# Revit family: 00-7906-05-00
name_source: partatom
category: Luminarias
revit_build: Autodesk Revit 2017 (Build: 20160225_1515(x64)
units: mm (PartAtom-declared; Revit-internal decimal feet)

## family parameters
Anfitrión = Cara
Compartido = Sí
Corte con vacíos al cargar = No
Cota de conector redondo = Diámetro de uso
Número OmniClass = 23.80.70.00
Origen de luz = No
Punto de cálculo de habitación = No
Tipo de pieza = Normal
Título OmniClass = Lighting

## types (1)
- 00-7906-05-00
    Acabado = Negro
    CRI = 90
    Carga aparente = 0 VA
    Catálogo = Decorative
    CodigoGubimclass = 50.60.50.20
    CodigoOmniclass = 21-04 50 40
    CodigoUniclass2015 = EF_70_80
    CodigoUniformat2010 = D5040
    DescripcionGubimclass = Iluminación interior
    DescripcionOmniclass = Lighting
    DescripcionUniclass2015 = Lighting
    DescripcionUniformat2010 = Lighting
    EAN13 = 8435575347298
    Eficiencia energética = LED A++
    Elevación por defecto = 1000 mm  [stored 3.28084 ft]
    Etiqueta V/f = 48 VDC
    Fabricante = LEDS C4
    Familia = Punto Low Voltage
    FechaVersion = Julio 2020
    Ficha = http://files.leds-c4.com
    Fotometría = http://files.leds-c4.com
    IMC = http://files.leds-c4.com
    IP = IP20
    IfcExportAs = IfcLightFixture
IfcLightFixture
    IfcExportType = NOTDEFINED
    Imagen web = http://files.leds-c4.com
    LDT = http://files.leds-c4.com
    Lumenes reales (lm) = 329
    Material = Aluminio
    Peso neto (KG) = 0.17
    Producto descatalogado = Catalogado ES
    Rayo de luz = EXTRA MEDIUM
    Referencia = 00-7906-05-00
    Temperatura color led (K) = Blanco cálido - 3000K
    Tender text (Castellano) = LEDS C4
Punto Low Voltage
00-7906-05-00

de uso interior para iluminar hacia abajo. 
Material estructura: Aluminio. Acabado estructura: Negro. Garantía: 5 Años.

Peso neto del producto (Kg): 0.170
Anchura o diámetro del producto (mm): 50
Altura del producto (mm): 1000

Clase 3. IP: IP20. LED. Nº de portalámparas o Leds: 1. Marca del LED: BRIDGELUX. Marca del Driver: TITANIC. Potencia máxima de la fuente de luz: 5W. Temperatura de color: Blanco cálido - 3000K. Índice de reproducción cromática: 90. Steps Mac Adam: 3. Diámetro máximo de la bombilla que admite la luminaria: 50.000h L80B20. UGR:  11.6. Riesgo fotobiológico: RG1. Flujo real (lm): 329. Lm/W reales: 51. Rango de voltaje/frecuencia: 24-48. Voltaje: 8.5. Equipo incluido: No. Potencia total: 6.5.
    Tender text (English) = LEDS C4
Punto Low Voltage
00-7906-05-00

for indoor use. 

For downlighting. Structure material: Aluminium. Structure finish: Black. Warranty: 5 Years.

Product net weight (Kg): 0.170
Product width or diameter (mm): 50
Product height (mm): 1000

Class 3. IP: IP20. LED. No. of lampholders or LEDs: 1. LED brand: BRIDGELUX. Driver brand: TITANIC. Maximum power of light source: 5W. Colour temperature: LED warm-white 3000K. Colour rendering index: 90. MacAdam Steps: 3. Maximum diameter of luminaire bulb: 50.000h L80B20. UGR:  11.6. Photobiological risk: RG1. Real flux (lm): 329. Lm/Real W: 51. Voltage and frequency range: 24-48. Voltage: 8.5. Gear included: No. Total power: 6.5.
    Tipo = Bajo Voltage
    Vatios (W) = 6.5
    Versión = v1

note: [stored X ft] marks values corroborated as IEEE doubles in the binary element streams (Revit-internal decimal feet)
